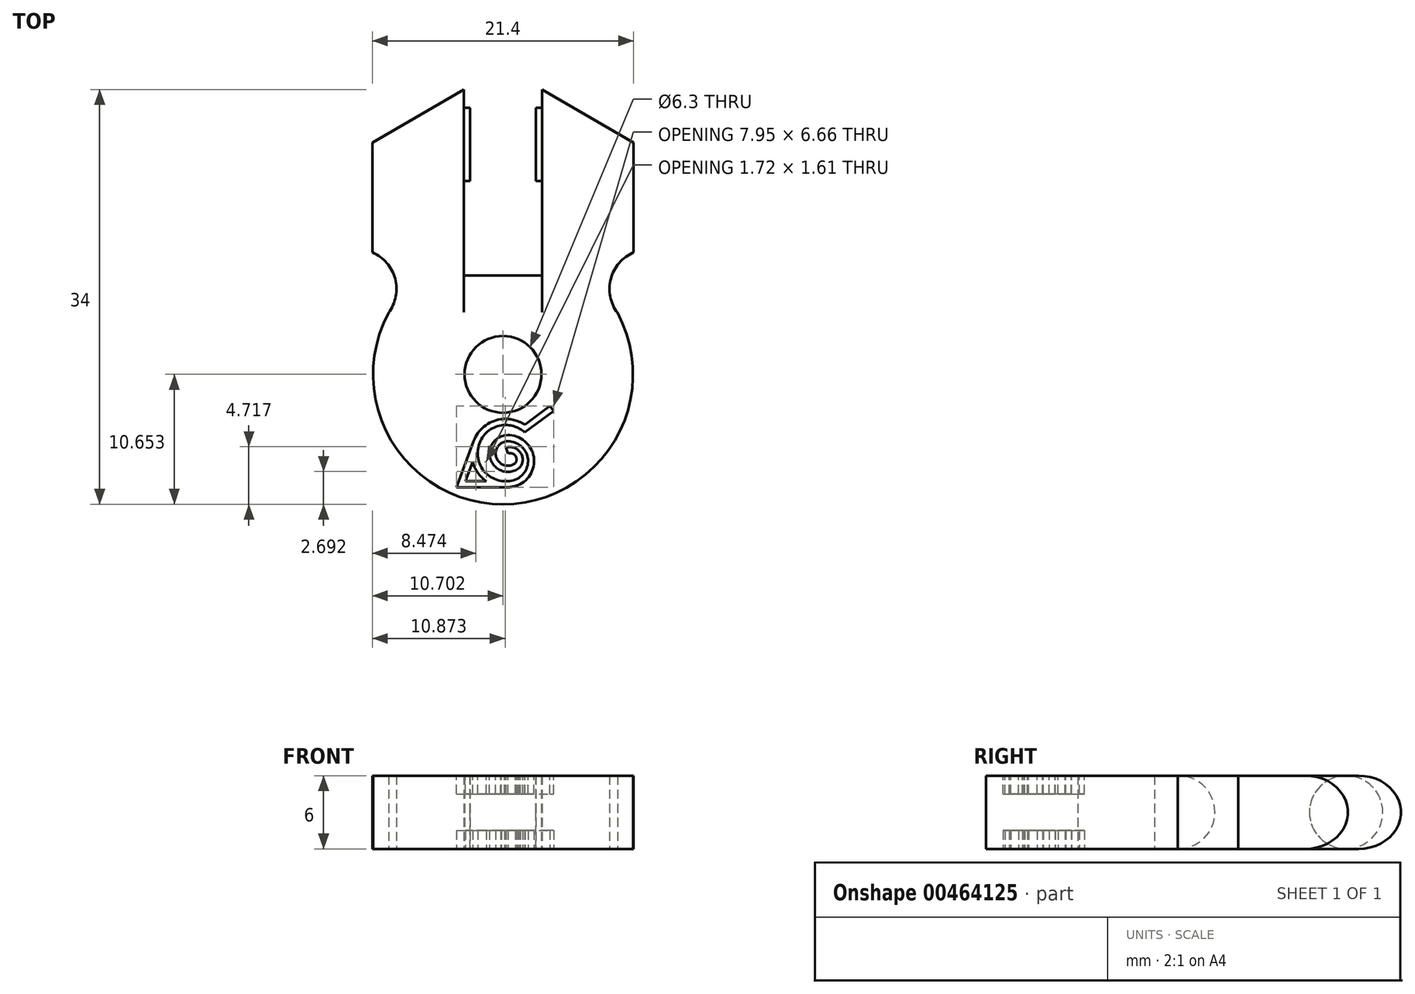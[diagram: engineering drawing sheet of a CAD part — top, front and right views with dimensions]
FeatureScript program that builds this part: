
annotation { "Feature Type Name" : "Feature", "Feature Type Description" : "" }
export const myFeature = defineFeature(function(context is Context, id is Id, definition is map)
    precondition{}
    {
        {
            var Q0;
            Q0=qCreatedBy(makeId("Top.planeOp"),FACE);
            var sketch = newSketch(context, id + "F0", { "sketchPlane" : qUnion([Q0])});
            skCircle(sketch, "E0", {"center": v(-10.56, -6.9) * mm, "radius": 10.65 * mm});
            skCircle(sketch, "E1", {"center": v(-10.56, -6.9) * mm, "radius": 3.15 * mm});
            skLineSegment(sketch, "E2", {"start": v(-10.56, -6.9) * mm, "end": v(-10.56, 3.74) * mm});
            skLineSegment(sketch, "E3", {"start": v(-13.76, 1.2) * mm, "end": v(-7.36, 1.2) * mm});
            skLineSegment(sketch, "E4", {"start": v(-13.76, 1.2) * mm, "end": v(-13.76, 16.44) * mm});
            skLineSegment(sketch, "E5", {"start": v(-7.36, 1.2) * mm, "end": v(-7.36, 16.44) * mm});
            skLineSegment(sketch, "E6", {"start": v(-7.36, 16.44) * mm, "end": v(0.14, 12.1) * mm});
            skLineSegment(sketch, "E7", {"start": v(-13.76, 16.44) * mm, "end": v(-21.26, 12.1) * mm});
            skLineSegment(sketch, "E8", {"start": v(-21.26, 12.1) * mm, "end": v(-21.26, 3.1) * mm});
            skLineSegment(sketch, "E9", {"start": v(0.14, 12.1) * mm, "end": v(0.14, 3.1) * mm});
            skLineSegment(sketch, "E10", {"start": v(-21.26, 12.1) * mm, "end": v(-21.26, 16.44) * mm});
            skLineSegment(sketch, "E11", {"start": v(-21.26, 16.44) * mm, "end": v(-13.76, 16.44) * mm});
            skArc(sketch, "E12", {"start": v(-19.94, -1.86) * mm, "mid": v(-19.4, 0.93) * mm, "end": v(-21.26, 3.1) * mm});
            skArc(sketch, "E13", {"start": v(0.14, 3.1) * mm, "mid": v(-1.72, 0.93) * mm, "end": v(-1.18, -1.86) * mm});
            skSolve(sketch);
        }
        {
            var Q0;
            {var subQ0=sQuery(id+"F0.wireOp",EDGE,"E7");Q0=makeQuery(id+"F0.imprint","IMPRINT",FACE,{"disambiguationData":[TD([[makeQuery(id+"F0.imprint","IMPRINT",EDGE,{"derivedFrom":subQ0}),1.0]])]});}
            var Q1;
            Q1=makeQuery(id+"F0.imprint","IMPRINT",FACE,{"disambiguationData":[TD([[makeQuery(id+"F0.imprint","IMPRINT",EDGE,{"derivedFrom":sQuery(id+"F0.wireOp",EDGE,"E1")}),-1.0]])]});
            var Q2;
            {var subQ1=sQuery(id+"F0.wireOp",EDGE,"E6");Q2=makeQuery(id+"F0.imprint","IMPRINT",FACE,{"disambiguationData":[TD([[makeQuery(id+"F0.imprint","IMPRINT",EDGE,{"derivedFrom":subQ1}),-1.0]])]});}
            extrude(context, id + "F1", {"entities" : qUnion([Q0, Q1, Q2]), "depth" : 6 * mm});
        }
        {
            var Q0;
            Q0=makeQuery(id+"F1.opExtrude","SWEPT_FACE",FACE,{"disambiguationData":[OSD([sQuery(id+"F0.wireOp",EDGE,"E4")])]});
            var sketch = newSketch(context, id + "F2", { "sketchPlane" : qUnion([Q0])});
            skCircle(sketch, "E14", {"center": v(11.94, 3) * mm, "radius": 3 * mm});
            skSolve(sketch);
        }
        {
            var Q0;
            {var subQ0=sQuery(id+"F2.wireOp",EDGE,"E14");var subQ1=sQuery(id+"F0.wireOp",EDGE,"E4");var subQ2=makeQuery(id+"F2.imprint","INTERSECT",VERTEX,{"derivedFrom":[makeQuery(id+"F1.opExtrude","CAP_EDGE",EDGE,{"disambiguationData":[OSD([subQ1])],"isStart":true}),subQ0]});Q0=makeQuery(id+"F2.imprint","IMPRINT",FACE,{"disambiguationData":[TD([[makeQuery(id+"F2.imprint","IMPRINT",EDGE,{"disambiguationData":[TD([[subQ2,1.0]])],"derivedFrom":subQ0}),1.0]])]});}
            extrude(context, id + "F3", {"entities" : qUnion([Q0]), "operationType" : NewBodyOperationType.ADD, "depth" : .5 * mm});
        }
        {
            var Q0;
            Q0=makeQuery(id+"F1.opExtrude","SWEPT_FACE",FACE,{"disambiguationData":[OSD([sQuery(id+"F0.wireOp",EDGE,"E5")])]});
            var sketch = newSketch(context, id + "F4", { "sketchPlane" : qUnion([Q0])});
            skCircle(sketch, "E15", {"center": v(-11.94, 3) * mm, "radius": 3 * mm});
            skSolve(sketch);
        }
        {
            var Q0;
            {var subQ0=sQuery(id+"F4.wireOp",EDGE,"E15");var subQ1=sQuery(id+"F0.wireOp",EDGE,"E5");var subQ2=makeQuery(id+"F4.imprint","INTERSECT",VERTEX,{"derivedFrom":[makeQuery(id+"F1.opExtrude","CAP_EDGE",EDGE,{"disambiguationData":[OSD([subQ1])],"isStart":true}),subQ0]});Q0=makeQuery(id+"F4.imprint","IMPRINT",FACE,{"disambiguationData":[TD([[makeQuery(id+"F4.imprint","IMPRINT",EDGE,{"disambiguationData":[TD([[subQ2,1.0]])],"derivedFrom":subQ0}),1.0]])]});}
            extrude(context, id + "F5", {"entities" : qUnion([Q0]), "operationType" : NewBodyOperationType.ADD, "depth" : .5 * mm});
        }
        {
            var Q0;
            Q0=makeQuery(id+"F1.opExtrude","CAP_EDGE",EDGE,{"disambiguationData":[OSD([sQuery(id+"F0.wireOp",EDGE,"E3")])],"isStart":true});
            var Q1;
            Q1=makeQuery(id+"F1.opExtrude","CAP_EDGE",EDGE,{"disambiguationData":[OSD([sQuery(id+"F0.wireOp",EDGE,"E3")])],"isStart":false});
            fillet(context, id + "F6", {"entities" : qUnion([Q0, Q1]), "radius" : 3 * mm, "tangentPropagation" : true, "allowEdgeOverflow" : false});
        }
        {
            var Q0;
            Q0=makeQuery(id+"F1.opExtrude","CAP_EDGE",EDGE,{"disambiguationData":[OSD([sQuery(id+"F0.wireOp",EDGE,"E6")])],"isStart":false});
            var Q1;
            Q1=makeQuery(id+"F1.opExtrude","CAP_EDGE",EDGE,{"disambiguationData":[OSD([sQuery(id+"F0.wireOp",EDGE,"E6")])],"isStart":true});
            var Q2;
            Q2=makeQuery(id+"F1.opExtrude","CAP_EDGE",EDGE,{"disambiguationData":[OSD([sQuery(id+"F0.wireOp",EDGE,"E7")])],"isStart":false});
            var Q3;
            Q3=makeQuery(id+"F1.opExtrude","CAP_EDGE",EDGE,{"disambiguationData":[OSD([sQuery(id+"F0.wireOp",EDGE,"E7")])],"isStart":true});
            fillet(context, id + "F7", {"entities" : qUnion([Q0, Q1, Q2, Q3]), "radius" : 3 * mm, "tangentPropagation" : true, "allowEdgeOverflow" : false});
        }
        {
            var Q0;
            Q0=makeQuery(id+"F1.opExtrude","CAP_FACE",FACE,{"disambiguationData":[OSD([sQuery(id+"F0.wireOp",EDGE,"E0"),sQuery(id+"F0.wireOp",EDGE,"E1"),sQuery(id+"F0.wireOp",EDGE,"E3"),sQuery(id+"F0.wireOp",EDGE,"E4"),sQuery(id+"F0.wireOp",EDGE,"E5"),sQuery(id+"F0.wireOp",EDGE,"E6"),sQuery(id+"F0.wireOp",EDGE,"E7"),sQuery(id+"F0.wireOp",EDGE,"E8"),sQuery(id+"F0.wireOp",EDGE,"E9"),sQuery(id+"F0.wireOp",EDGE,"E12"),sQuery(id+"F0.wireOp",EDGE,"E13")])],"isStart":false});
            var sketch = newSketch(context, id + "F8", { "sketchPlane" : qUnion([Q0])});
            skArc(sketch, "E16", {"start": v(-9.54, -15.53) * mm, "mid": v(-8.56, -13.62) * mm, "end": v(-10.33, -12.4) * mm});
            skArc(sketch, "E17", {"start": v(-10.68, -11.08) * mm, "mid": v(-12.57, -13.94) * mm, "end": v(-9.54, -15.53) * mm});
            skLineSegment(sketch, "E18", {"start": v(-11.93, -15.67) * mm, "end": v(-13.64, -15.67) * mm});
            skLineSegment(sketch, "E19", {"start": v(-13.64, -15.67) * mm, "end": v(-13.05, -14.06) * mm});
            skArc(sketch, "E20", {"start": v(-10.33, -12.4) * mm, "mid": v(-11.07, -13.8) * mm, "end": v(-9.54, -14.19) * mm});
            skArc(sketch, "E21", {"start": v(-8.77, -11.66) * mm, "mid": v(-9.66, -11.16) * mm, "end": v(-10.68, -11.08) * mm});
            skArc(sketch, "E22", {"start": v(-9.54, -14.19) * mm, "mid": v(-9.56, -13.57) * mm, "end": v(-10.15, -13.4) * mm});
            skLineSegment(sketch, "E23", {"start": v(-8.77, -11.66) * mm, "end": v(-6.41, -9.92) * mm});
            skArc(sketch, "E24.0", {"start": v(-8.77, -11.04) * mm, "mid": v(-9.72, -10.63) * mm, "end": v(-10.75, -10.58) * mm});
            skArc(sketch, "E25.0", {"start": v(-10.76, -10.59) * mm, "mid": v(-12.1, -11.19) * mm, "end": v(-12.96, -12.39) * mm});
            skLineSegment(sketch, "E26.0", {"start": v(-14.11, -15.5) * mm, "end": v(-12.96, -12.39) * mm});
            skLineSegment(sketch, "E27.0", {"start": v(-10.33, -16.17) * mm, "end": v(-13.64, -16.17) * mm});
            skArc(sketch, "E28.0", {"start": v(-9.36, -16) * mm, "mid": v(-8.07, -13.5) * mm, "end": v(-10.4, -11.9) * mm});
            skArc(sketch, "E29.0", {"start": v(-10.42, -11.91) * mm, "mid": v(-11.53, -14) * mm, "end": v(-9.23, -14.58) * mm});
            skArc(sketch, "E30.0", {"start": v(-9.12, -14.46) * mm, "mid": v(-9.17, -13.26) * mm, "end": v(-10.32, -12.92) * mm});
            skArc(sketch, "E31", {"start": v(-9.23, -14.58) * mm, "mid": v(-9.17, -14.53) * mm, "end": v(-9.12, -14.46) * mm});
            skLineSegment(sketch, "E32", {"start": v(-10.32, -12.92) * mm, "end": v(-10.15, -13.4) * mm});
            skLineSegment(sketch, "E33.0", {"start": v(-8.77, -11.04) * mm, "end": v(-6.7, -9.51) * mm});
            skLineSegment(sketch, "E34", {"start": v(-6.7, -9.51) * mm, "end": v(-6.41, -9.92) * mm});
            skLineSegment(sketch, "E35", {"start": v(-14.11, -15.5) * mm, "end": v(-14.36, -16.17) * mm});
            skLineSegment(sketch, "E36", {"start": v(-14.36, -16.17) * mm, "end": v(-13.64, -16.17) * mm});
            skArc(sketch, "E37.trimOffspring", {"start": v(-10.33, -16.17) * mm, "mid": v(-9.84, -16.13) * mm, "end": v(-9.37, -16) * mm});
            skArc(sketch, "E38.trimOffspring", {"start": v(-13.05, -14.06) * mm, "mid": v(-12.63, -14.97) * mm, "end": v(-11.93, -15.67) * mm});
            skArc(sketch, "E39", {"start": v(-10.76, -10.59) * mm, "mid": v(-10.75, -10.59) * mm, "end": v(-10.75, -10.58) * mm});
            skArc(sketch, "E40", {"start": v(-9.37, -16) * mm, "mid": v(-9.36, -16) * mm, "end": v(-9.36, -16) * mm});
            skArc(sketch, "E41", {"start": v(-10.4, -11.9) * mm, "mid": v(-10.4, -11.9) * mm, "end": v(-10.42, -11.91) * mm});
            skSolve(sketch);
        }
        {
            var Q0;
            Q0 = qSketchRegion(id + "F8", true);
            extrude(context, id + "F9", {"entities" : qUnion([Q0]), "operationType" : NewBodyOperationType.REMOVE, "oppositeDirection" : true, "depth" : 1.5 * mm});
        }
        {
            var Q0;
            Q0=makeQuery(id+"F1.opExtrude","CAP_FACE",FACE,{"disambiguationData":[OSD([sQuery(id+"F0.wireOp",EDGE,"E0"),sQuery(id+"F0.wireOp",EDGE,"E1"),sQuery(id+"F0.wireOp",EDGE,"E3"),sQuery(id+"F0.wireOp",EDGE,"E4"),sQuery(id+"F0.wireOp",EDGE,"E5"),sQuery(id+"F0.wireOp",EDGE,"E6"),sQuery(id+"F0.wireOp",EDGE,"E7"),sQuery(id+"F0.wireOp",EDGE,"E8"),sQuery(id+"F0.wireOp",EDGE,"E9"),sQuery(id+"F0.wireOp",EDGE,"E12"),sQuery(id+"F0.wireOp",EDGE,"E13")])],"isStart":true});
            var sketch = newSketch(context, id + "F10", { "sketchPlane" : qUnion([Q0])});
            skPoint(sketch, "E42.0", {"position": v(-7.74, 10.27) * mm});
            skLineSegment(sketch, "E43.0", {"start": v(-8.77, 11.66) * mm, "end": v(-6.41, 9.92) * mm});
            skLineSegment(sketch, "E44.0", {"start": v(-14.36, 16.17) * mm, "end": v(-12.96, 12.39) * mm});
            skLineSegment(sketch, "E45.0.0", {"start": v(-14.36, 16.17) * mm, "end": v(-10.33, 16.17) * mm});
            skArc(sketch, "E45.0.1", {"start": v(-10.33, 16.17) * mm, "mid": v(-9.84, 16.13) * mm, "end": v(-9.37, 16) * mm});
            skArc(sketch, "E45.0.2", {"start": v(-9.37, 16) * mm, "mid": v(-9.36, 16) * mm, "end": v(-9.36, 16) * mm});
            skArc(sketch, "E45.0.3", {"start": v(-9.36, 16) * mm, "mid": v(-8.07, 13.5) * mm, "end": v(-10.4, 11.9) * mm});
            skArc(sketch, "E45.0.4", {"start": v(-10.4, 11.9) * mm, "mid": v(-10.4, 11.9) * mm, "end": v(-10.42, 11.91) * mm});
            skArc(sketch, "E45.0.5", {"start": v(-10.42, 11.91) * mm, "mid": v(-11.53, 14) * mm, "end": v(-9.23, 14.58) * mm});
            skArc(sketch, "E45.0.6", {"start": v(-9.23, 14.58) * mm, "mid": v(-9.17, 14.53) * mm, "end": v(-9.12, 14.46) * mm});
            skArc(sketch, "E45.0.7", {"start": v(-9.12, 14.46) * mm, "mid": v(-9.17, 13.26) * mm, "end": v(-10.32, 12.92) * mm});
            skLineSegment(sketch, "E45.0.8", {"start": v(-10.32, 12.92) * mm, "end": v(-10.15, 13.4) * mm});
            skArc(sketch, "E45.0.9", {"start": v(-10.15, 13.4) * mm, "mid": v(-9.56, 13.57) * mm, "end": v(-9.54, 14.19) * mm});
            skArc(sketch, "E45.0.10", {"start": v(-9.54, 14.19) * mm, "mid": v(-11.07, 13.8) * mm, "end": v(-10.33, 12.4) * mm});
            skArc(sketch, "E45.0.11", {"start": v(-10.33, 12.4) * mm, "mid": v(-8.56, 13.62) * mm, "end": v(-9.54, 15.53) * mm});
            skArc(sketch, "E45.0.12", {"start": v(-9.54, 15.53) * mm, "mid": v(-12.57, 13.94) * mm, "end": v(-10.68, 11.08) * mm});
            skArc(sketch, "E45.0.13", {"start": v(-10.68, 11.08) * mm, "mid": v(-9.66, 11.16) * mm, "end": v(-8.77, 11.66) * mm});
            skLineSegment(sketch, "E45.0.15", {"start": v(-6.41, 9.92) * mm, "end": v(-6.7, 9.51) * mm});
            skLineSegment(sketch, "E45.0.16", {"start": v(-6.7, 9.51) * mm, "end": v(-8.77, 11.04) * mm});
            skArc(sketch, "E45.0.17", {"start": v(-8.77, 11.04) * mm, "mid": v(-9.72, 10.63) * mm, "end": v(-10.75, 10.58) * mm});
            skArc(sketch, "E45.0.18", {"start": v(-10.75, 10.58) * mm, "mid": v(-10.75, 10.59) * mm, "end": v(-10.76, 10.59) * mm});
            skArc(sketch, "E45.0.19", {"start": v(-10.76, 10.59) * mm, "mid": v(-12.1, 11.19) * mm, "end": v(-12.96, 12.39) * mm});
            skLineSegment(sketch, "E45.0.20", {"start": v(-12.96, 12.39) * mm, "end": v(-14.36, 16.17) * mm});
            skLineSegment(sketch, "E46.0.0", {"start": v(-13.05, 14.06) * mm, "end": v(-13.64, 15.67) * mm});
            skLineSegment(sketch, "E46.0.1", {"start": v(-13.64, 15.67) * mm, "end": v(-11.93, 15.67) * mm});
            skArc(sketch, "E46.0.2", {"start": v(-11.93, 15.67) * mm, "mid": v(-12.63, 14.97) * mm, "end": v(-13.05, 14.06) * mm});
            skSolve(sketch);
        }
        {
            var Q0;
            Q0=makeQuery(id+"F10.imprint","IMPRINT",FACE,{"disambiguationData":[TD([[makeQuery(id+"F10.imprint","IMPRINT",EDGE,{"derivedFrom":sQuery(id+"F10.wireOp",EDGE,"E45.0.0")}),-1.0]])]});
            extrude(context, id + "F11", {"entities" : qUnion([Q0]), "operationType" : NewBodyOperationType.REMOVE, "oppositeDirection" : true, "depth" : 1.5 * mm});
        }
    });
